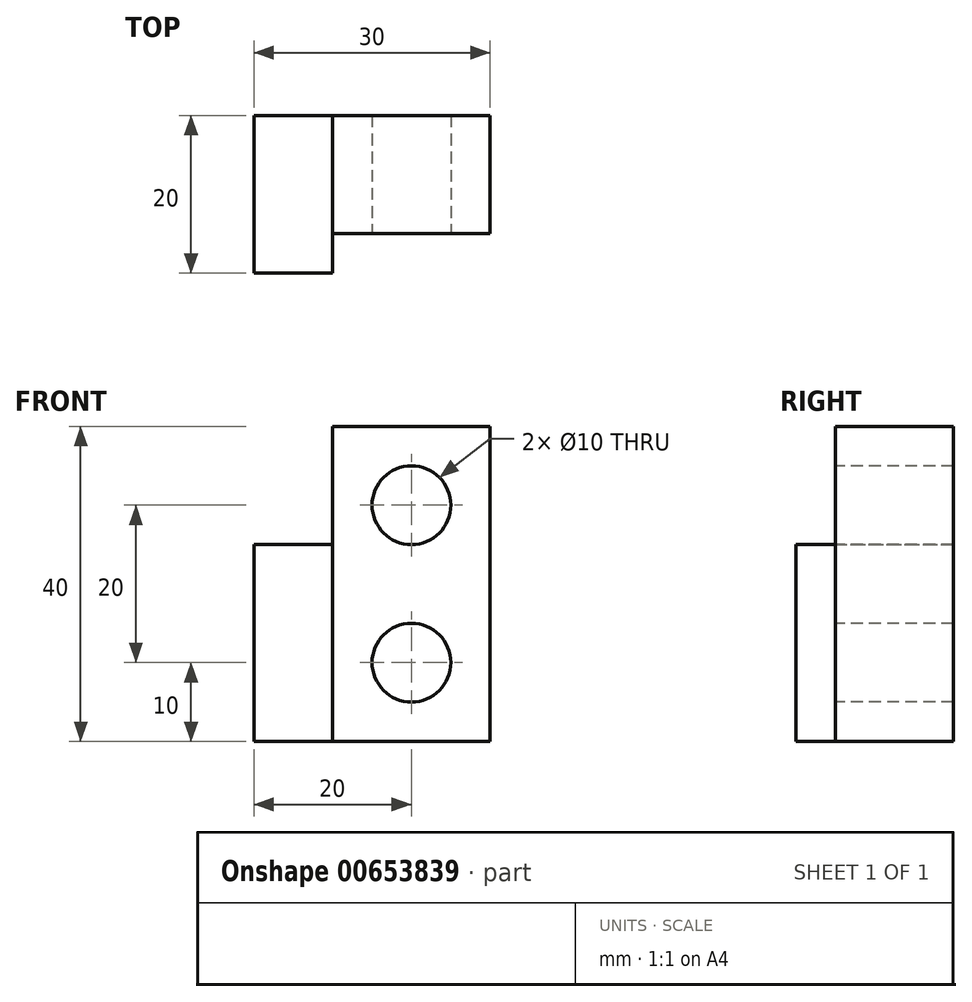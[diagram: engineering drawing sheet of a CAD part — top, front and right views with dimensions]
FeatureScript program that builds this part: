
annotation { "Feature Type Name" : "Feature", "Feature Type Description" : "" }
export const myFeature = defineFeature(function(context is Context, id is Id, definition is map)
    precondition{}
    {
        {
            var Q0;
            Q0=qCreatedBy(makeId("Front.planeOp"),FACE);
            var sketch = newSketch(context, id + "F0", { "sketchPlane" : qUnion([Q0])});
            skLineSegment(sketch, "E0.bottom", {"start": v(-10, 20) * mm, "end": v(10, 20) * mm});
            skLineSegment(sketch, "E0.top", {"start": v(-10, -20) * mm, "end": v(10, -20) * mm});
            skLineSegment(sketch, "E0.left", {"start": v(-10, 20) * mm, "end": v(-10, -20) * mm});
            skLineSegment(sketch, "E0.right", {"start": v(10, 20) * mm, "end": v(10, -20) * mm});
            skPoint(sketch, "E0.middle", {"position": v(0, 0) * mm});
            skSolve(sketch);
        }
        {
            var Q0;
            Q0=qCreatedBy(makeId("Front.planeOp"),FACE);
            var sketch = newSketch(context, id + "F1", { "sketchPlane" : qUnion([Q0])});
            skLineSegment(sketch, "E1.bottom", {"start": v(-10, -20) * mm, "end": v(-20, -20) * mm});
            skLineSegment(sketch, "E1.top", {"start": v(-10, 5) * mm, "end": v(-20, 5) * mm});
            skLineSegment(sketch, "E1.left", {"start": v(-10, -20) * mm, "end": v(-10, 5) * mm});
            skLineSegment(sketch, "E1.right", {"start": v(-20, -20) * mm, "end": v(-20, 5) * mm});
            skSolve(sketch);
        }
        {
            var Q0;
            Q0=makeQuery(id+"F0.imprint","IMPRINT",FACE,{"disambiguationData":[TD([[makeQuery(id+"F0.imprint","IMPRINT",EDGE,{"derivedFrom":sQuery(id+"F0.wireOp",EDGE,"E0.bottom")}),-1.0]])]});
            extrude(context, id + "F2", {"entities" : qUnion([Q0]), "depth" : 15 * mm, "offsetDistance" : 25 * mm});
        }
        {
            var Q0;
            Q0=makeQuery(id+"F1.imprint","IMPRINT",FACE,{"disambiguationData":[TD([[makeQuery(id+"F1.imprint","IMPRINT",EDGE,{"derivedFrom":sQuery(id+"F1.wireOp",EDGE,"E1.bottom")}),-1.0]])]});
            extrude(context, id + "F3", {"entities" : qUnion([Q0]), "operationType" : NewBodyOperationType.ADD, "depth" : 20 * mm, "offsetDistance" : 25 * mm});
        }
        {
            var Q0;
            Q0=makeQuery(id+"F2.opExtrude","CAP_FACE",FACE,{"disambiguationData":[OSD([sQuery(id+"F0.wireOp",EDGE,"E0.bottom"),sQuery(id+"F0.wireOp",EDGE,"E0.top"),sQuery(id+"F0.wireOp",EDGE,"E0.left"),sQuery(id+"F0.wireOp",EDGE,"E0.right")])],"isStart":false});
            var sketch = newSketch(context, id + "F4", { "sketchPlane" : qUnion([Q0])});
            skCircle(sketch, "E2", {"center": v(0, 10) * mm, "radius": 5 * mm});
            skCircle(sketch, "E3", {"center": v(0, -10) * mm, "radius": 5 * mm});
            skSolve(sketch);
        }
        {
            var Q0;
            Q0=makeQuery(id+"F4.imprint","IMPRINT",FACE,{"disambiguationData":[TD([[makeQuery(id+"F4.imprint","IMPRINT",EDGE,{"derivedFrom":sQuery(id+"F4.wireOp",EDGE,"E2")}),1.0]])]});
            var Q1;
            Q1=makeQuery(id+"F4.imprint","IMPRINT",FACE,{"disambiguationData":[TD([[makeQuery(id+"F4.imprint","IMPRINT",EDGE,{"derivedFrom":sQuery(id+"F4.wireOp",EDGE,"E3")}),1.0]])]});
            extrude(context, id + "F5", {"entities" : qUnion([Q0, Q1]), "operationType" : NewBodyOperationType.REMOVE, "oppositeDirection" : true, "depth" : 15 * mm, "offsetDistance" : 25 * mm});
        }
    });
